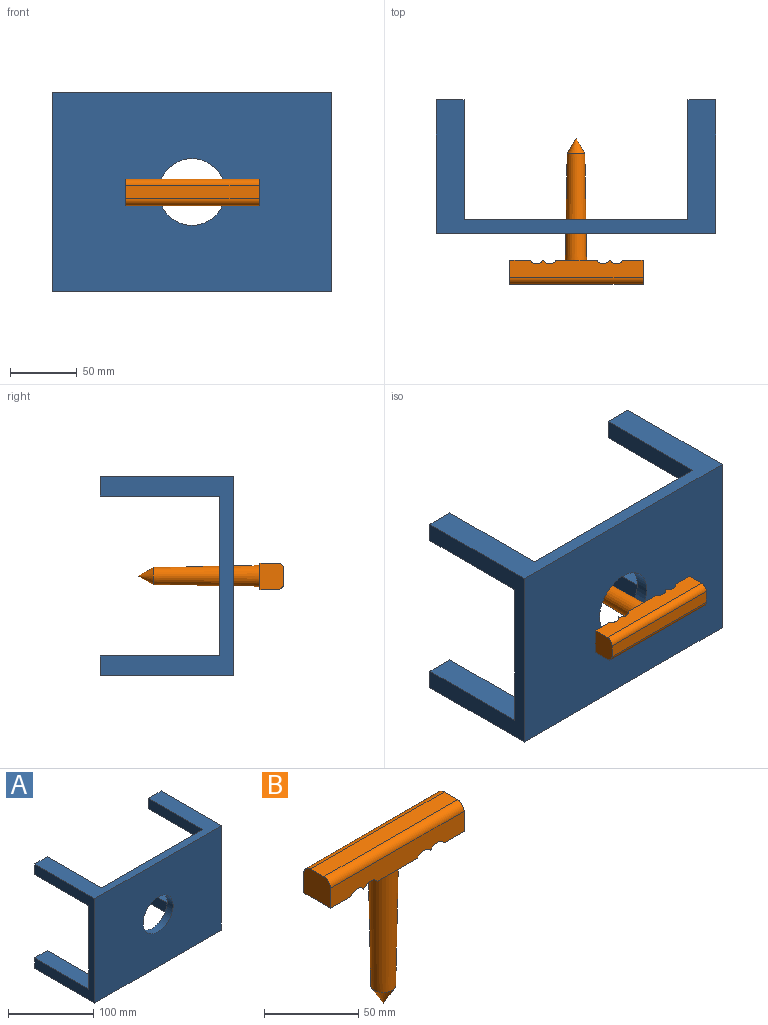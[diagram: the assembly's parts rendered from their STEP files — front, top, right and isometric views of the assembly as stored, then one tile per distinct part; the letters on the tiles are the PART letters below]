
ASSEMBLY  parts=2 mates=1
PART A: 19 faces, bbox 210x100x150 mm
  f0: plane 210x100mm, normal (0,0,-1), area 5880mm2, adj f1,f3,f5,f6,f13,f15,f17,f18
  f1: plane 150x100mm, normal (1,0,0), area 4200mm2, adj f0,f2,f5,f6,f11,f12,f16,f18
  f2: plane 210x100mm, normal (0,0,1), area 5880mm2, adj f1,f3,f5,f6,f7,f9,f10,f12
  f3: plane 150x100mm, normal (-1,0,0), area 4200mm2, adj f0,f2,f5,f6,f8,f9,f14,f15
  f4: cylinder r=25mm len=50mm, axis (0,-1,0), area 1570.8mm2, adj f5,f6
  f5: plane 210x150mm, normal (0,1,0), area 28276.5mm2, adj f0,f1,f2,f3,f4,f7,f8,f10
  f6: plane 210x150mm, normal (0,-1,0), area 29536.5mm2, adj f0,f1,f2,f3,f4
  f7: plane 90x15mm, normal (1,0,0), area 1350mm2, adj f2,f5,f8,f9
  f8: plane 90x21mm, normal (0,0,-1), area 1890mm2, adj f3,f5,f7,f9
  f9: plane 21x15mm, normal (0,1,0), area 315mm2, adj f2,f3,f7,f8
  f10: plane 90x15mm, normal (-1,0,0), area 1350mm2, adj f2,f5,f11,f12
  f11: plane 90x21mm, normal (0,0,-1), area 1890mm2, adj f1,f5,f10,f12
  f12: plane 21x15mm, normal (0,1,0), area 315mm2, adj f1,f2,f10,f11
  f13: plane 90x15mm, normal (1,0,0), area 1350mm2, adj f0,f5,f14,f15
  f14: plane 90x21mm, normal (0,0,1), area 1890mm2, adj f3,f5,f13,f15
  f15: plane 21x15mm, normal (0,1,0), area 315mm2, adj f0,f3,f13,f14
  f16: plane 90x21mm, normal (0,0,1), area 1890mm2, adj f1,f5,f17,f18
  f17: plane 90x15mm, normal (-1,0,0), area 1350mm2, adj f0,f5,f16,f18
  f18: plane 21x15mm, normal (0,1,0), area 315mm2, adj f0,f1,f16,f17
PART B: 16 faces, bbox 100x20x109.4 mm
  f0: plane 100x10mm, normal (0,0,1), area 1000mm2, adj f1,f9,f14,f15
  f1: plane 20x18mm, normal (-1,0,0), area 349.3mm2, adj f0,f2,f10,f11,f14,f15
  f2: plane 20x15mm, normal (0,0,-1), area 300mm2, adj f1,f3,f10,f11
  f3: cylinder r=6mm len=20mm, axis (0,1,0), area 236.4mm2, adj f2,f4,f10,f11
  f4: cylinder r=6mm len=20mm, axis (0,1,0), area 236.4mm2, adj f3,f5,f10,f11
  f5: plane 30x20mm, normal (0,0,-1), area 398.9mm2, adj f4,f6,f10,f11,f12
  f6: cylinder r=6mm len=20mm, axis (0,1,0), area 236.4mm2, adj f5,f7,f10,f11
  f7: cylinder r=6mm len=20mm, axis (0,1,0), area 236.4mm2, adj f6,f8,f10,f11
  f8: plane 20x15mm, normal (0,0,-1), area 300mm2, adj f7,f9,f10,f11
  f9: plane 20x18mm, normal (1,0,0), area 349.3mm2, adj f0,f8,f10,f11,f14,f15
  f10: plane 100x13mm, normal (0,-1,0), area 1224.5mm2, adj f1,f2,f3,f4,f5,f6,f7,f8
  f11: plane 100x13mm, normal (0,1,0), area 1224.5mm2, adj f1,f2,f3,f4,f5,f6,f7,f8
  f12: cone r=8mm half-angle=1deg, axis (0,0,1), area 3670.8mm2, adj f5,f13
  f13: cone r=6.6mm half-angle=30deg, axis (0,0,1), area 274mm2, adj f12
  f14: cylinder r=5mm len=100mm, axis (-1,0,0), area 785.4mm2, adj f0,f1,f9,f11
  f15: cylinder r=5mm len=100mm, axis (1,0,0), area 785.4mm2, adj f0,f1,f9,f10
PLACE A t=(2.92,-17.85,45.7)mm fixed
PLACE B rot(axis=(1,0,0),90deg) t=(-4.02,-65.53,55.45)mm
MATE slider B.f12 <-> A.f4  axis (0,-1,0) through (2.92,2.15,45.7)mm
